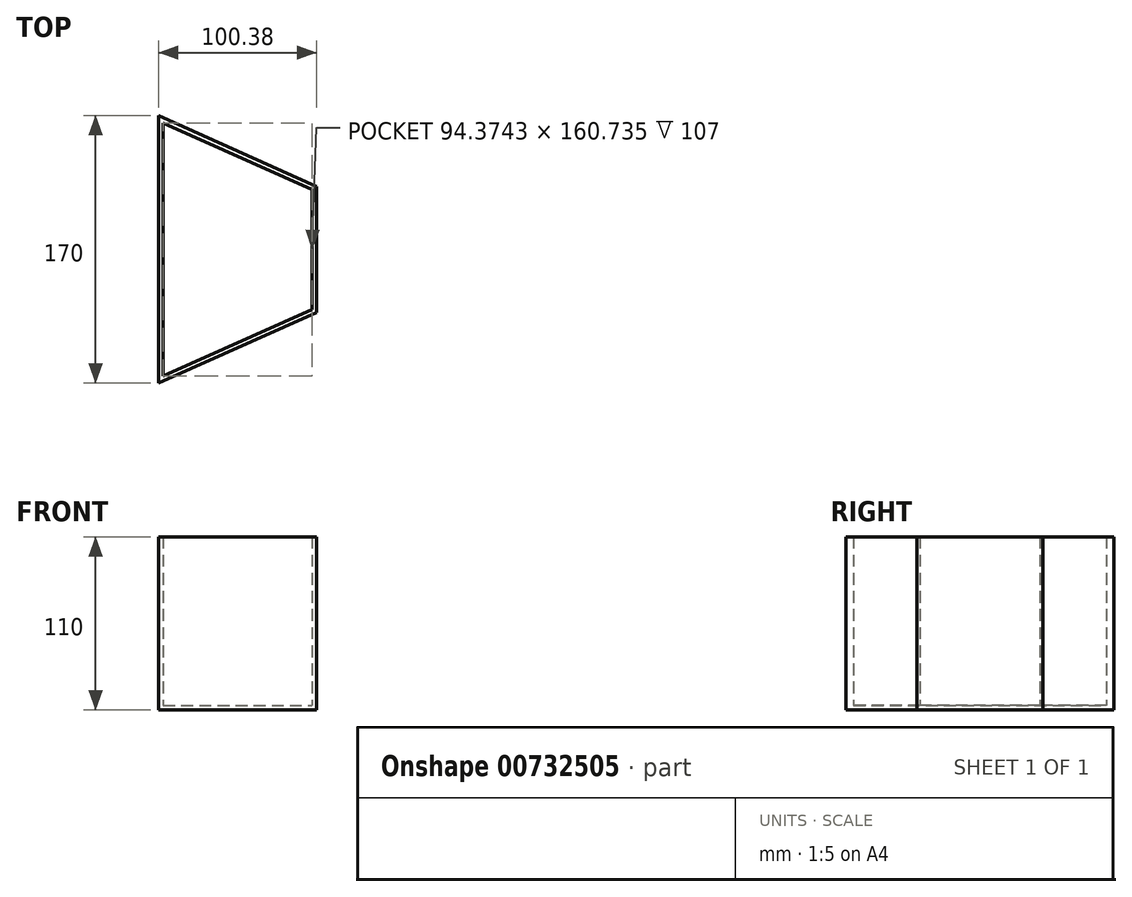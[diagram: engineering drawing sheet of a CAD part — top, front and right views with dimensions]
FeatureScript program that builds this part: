
annotation { "Feature Type Name" : "Feature", "Feature Type Description" : "" }
export const myFeature = defineFeature(function(context is Context, id is Id, definition is map)
    precondition{}
    {
        {
            var Q0;
            Q0=qCreatedBy(makeId("Top.planeOp"),FACE);
            var sketch = newSketch(context, id + "F0", { "sketchPlane" : qUnion([Q0])});
            skLineSegment(sketch, "E0", {"start": v(-116.4, 39.28) * mm, "end": v(-116.4, -130.72) * mm});
            skLineSegment(sketch, "E1", {"start": v(-116.4, -130.72) * mm, "end": v(-16.03, -85.72) * mm});
            skLineSegment(sketch, "E2", {"start": v(-16.03, -85.72) * mm, "end": v(-16.03, -5.72) * mm});
            skLineSegment(sketch, "E3", {"start": v(-16.03, -5.72) * mm, "end": v(-116.4, 39.28) * mm});
            skLineSegment(sketch, "E4", {"start": v(-16.03, -45.72) * mm, "end": v(-116.4, -45.72) * mm, "construction": true});
            skLineSegment(sketch, "E5", {"start": v(-113.4, 34.64) * mm, "end": v(-19.03, -7.67) * mm});
            skLineSegment(sketch, "E6", {"start": v(-19.03, -7.67) * mm, "end": v(-19.03, -83.78) * mm});
            skLineSegment(sketch, "E7", {"start": v(-19.03, -83.78) * mm, "end": v(-113.4, -126.1) * mm});
            skLineSegment(sketch, "E8", {"start": v(-113.4, -126.1) * mm, "end": v(-113.4, 34.64) * mm});
            skPoint(sketch, "E9", {"position": v(-113.4, -45.72) * mm});
            skSolve(sketch);
        }
        {
            var Q0;
            Q0 = qSketchRegion(id + "F0", true);
            extrude(context, id + "F1", {"entities" : qUnion([Q0]), "depth" : 110 * mm, "offsetDistance" : 25 * mm});
        }
        {
            var Q0;
            Q0=makeQuery(id+"F0.imprint","IMPRINT",FACE,{"disambiguationData":[TD([[makeQuery(id+"F0.imprint","IMPRINT",EDGE,{"derivedFrom":sQuery(id+"F0.wireOp",EDGE,"E5")}),-1.0]])]});
            extrude(context, id + "F2", {"entities" : qUnion([Q0]), "operationType" : NewBodyOperationType.ADD, "depth" : 3 * mm, "offsetDistance" : 25 * mm});
        }
    });
